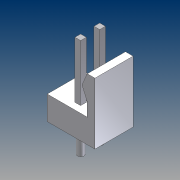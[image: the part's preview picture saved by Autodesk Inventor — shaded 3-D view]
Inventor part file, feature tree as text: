
AUTODESK INVENTOR PART (.ipt)
format: ipt  version: 2012 (Build 160160000, 160)  size: 110,592 bytes
history: native  units: mm (DEFAULTED — no unit token found)
features: extrude x3, plane x3, sketch x2, pattern_linear x1
ambient origin geometry x5: Origin, X Axis, Y Axis, Z Axis, Center Point
bodies: Solid1 (feature_tree)
feature tree (9):
  extrude  "Extrusion1"  Depth=3.175mm
  sketch  "Sketch3"  dims[d2=8.1788mm d3=1.4478mm d4=1.016mm d5=2.54mm d6=0.0mm d7=0.762mm d8=2.794mm d9=0.0mm d10=10.668mm d11=0.0mm d12=20.0mm d14=2.54mm d15=0.889mm]
  extrude  "Extrusion2"  Depth=1.4478mm
  extrude  "Extrusion3"  Depth=1.016mm
  pattern_linear  "Rectangular Pattern1"  Spacing1=2.54mm  [1 undecoded]
  plane  "YZ Plane (RIGHT)"
  plane  "XZ Plane (TOP)"
  plane  "XY Plane (FRONT)"
  sketch  "Sketch2"  dims[d0=6.35mm d1=3.175mm]
note: 1 required parameter value undecoded (feature->parameter linkage not recoverable at this tier; creation-order binding heuristic only, values carry confidence <= 0.55)
